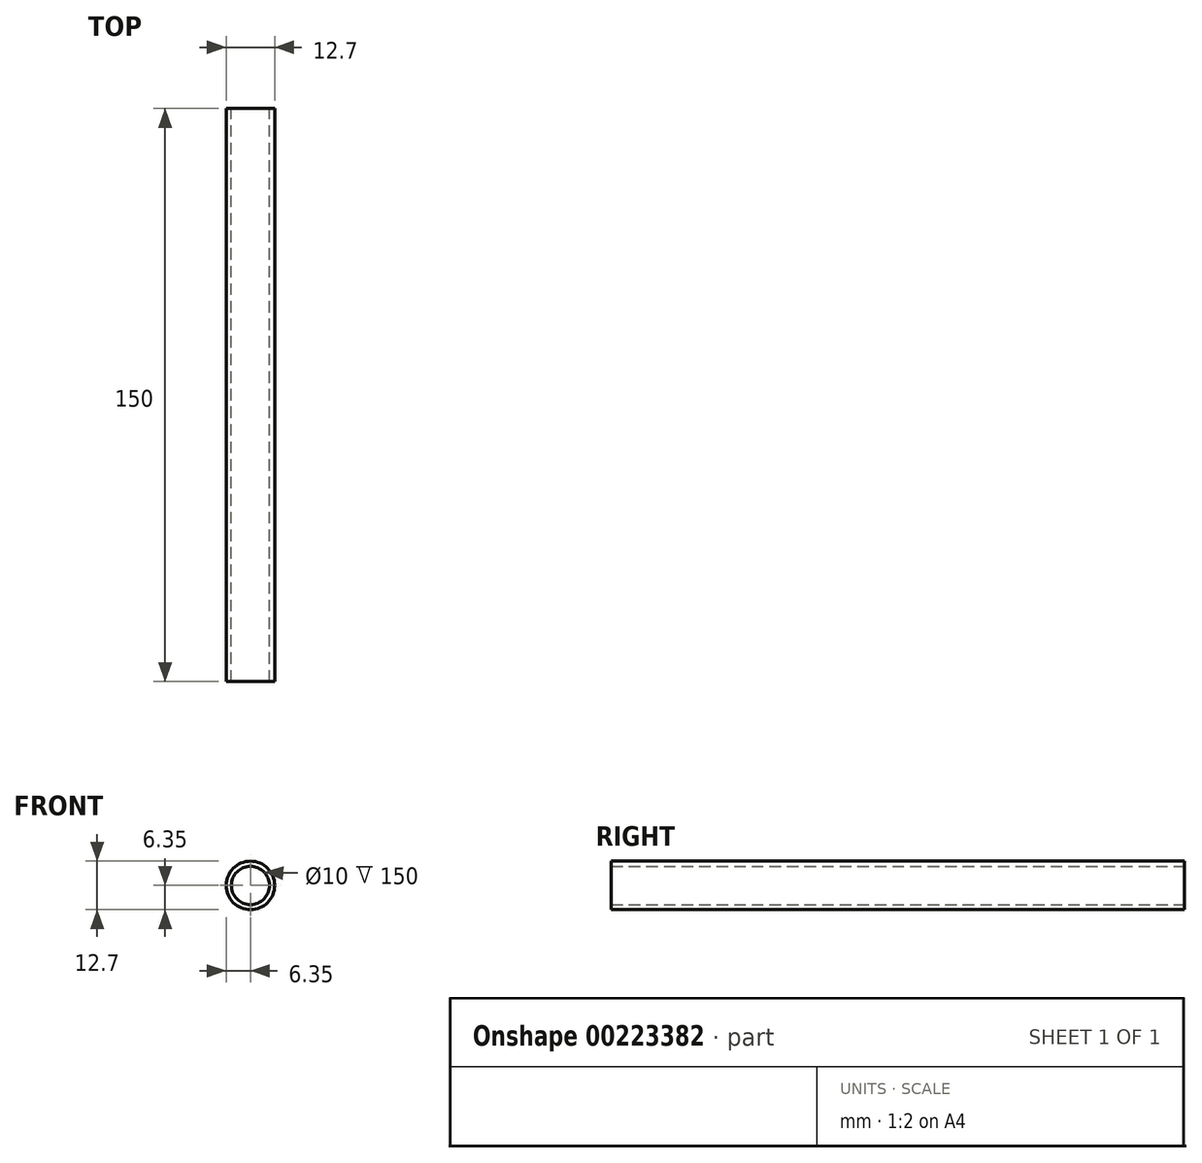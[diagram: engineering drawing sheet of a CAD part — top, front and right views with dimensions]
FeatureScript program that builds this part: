
annotation { "Feature Type Name" : "Feature", "Feature Type Description" : "" }
export const myFeature = defineFeature(function(context is Context, id is Id, definition is map)
    precondition{}
    {
        {
            var Q0;
            Q0=qCreatedBy(makeId("Front.planeOp"),FACE);
            var sketch = newSketch(context, id + "F0", { "sketchPlane" : qUnion([Q0])});
            skCircle(sketch, "E0", {"center": v(0, 0) * mm, "radius": 1.06 * mm});
            skCircle(sketch, "E1", {"center": v(0, 0) * mm, "radius": 6.35 * mm});
            skCircle(sketch, "E2", {"center": v(0, 0) * mm, "radius": 5 * mm});
            skSolve(sketch);
        }
        {
            var Q0;
            Q0=makeQuery(id+"F0.imprint","IMPRINT",FACE,{"disambiguationData":[TD([[makeQuery(id+"F0.imprint","IMPRINT",EDGE,{"derivedFrom":sQuery(id+"F0.wireOp",EDGE,"E1")}),1.0]])]});
            extrude(context, id + "F1", {"entities" : qUnion([Q0]), "depth" : 150 * mm});
        }
    });
